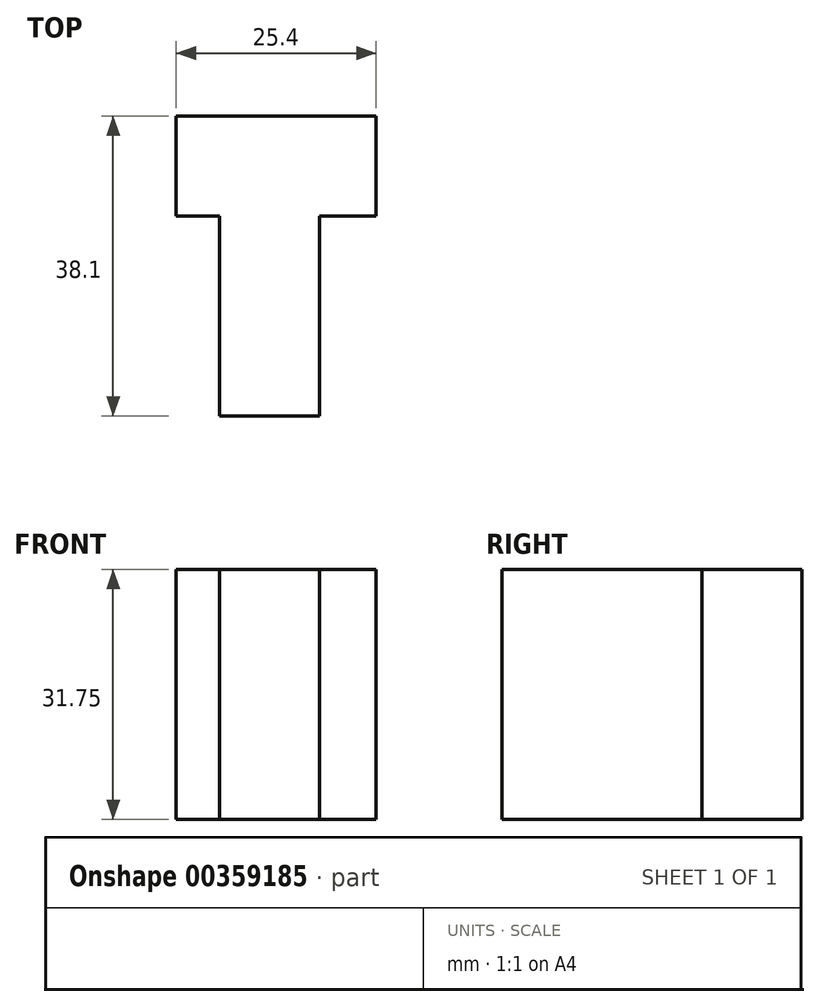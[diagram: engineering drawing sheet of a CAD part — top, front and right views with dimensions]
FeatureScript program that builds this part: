
annotation { "Feature Type Name" : "Feature", "Feature Type Description" : "" }
export const myFeature = defineFeature(function(context is Context, id is Id, definition is map)
    precondition{}
    {
        {
            var Q0;
            Q0=qCreatedBy(makeId("Top.planeOp"),FACE);
            var sketch = newSketch(context, id + "F0", { "sketchPlane" : qUnion([Q0])});
            skLineSegment(sketch, "E0", {"start": v(0, 0) * mm, "end": v(0, 25.4) * mm});
            skLineSegment(sketch, "E1", {"start": v(0, 25.4) * mm, "end": v(-5.5, 25.4) * mm});
            skLineSegment(sketch, "E2", {"start": v(-5.5, 25.4) * mm, "end": v(-5.5, 38.1) * mm});
            skLineSegment(sketch, "E3", {"start": v(-5.5, 38.1) * mm, "end": v(19.9, 38.1) * mm});
            skLineSegment(sketch, "E4", {"start": v(19.9, 38.1) * mm, "end": v(19.9, 25.4) * mm});
            skLineSegment(sketch, "E5", {"start": v(19.9, 25.4) * mm, "end": v(12.7, 25.4) * mm});
            skLineSegment(sketch, "E6", {"start": v(12.7, 25.4) * mm, "end": v(12.7, 0) * mm});
            skLineSegment(sketch, "E7", {"start": v(0, 0) * mm, "end": v(12.7, 0) * mm});
            skSolve(sketch);
        }
        {
            var Q0;
            Q0 = qSketchRegion(id + "F0", true);
            extrude(context, id + "F1", {"entities" : qUnion([Q0]), "depth" : 31.75 * mm});
        }
    });
